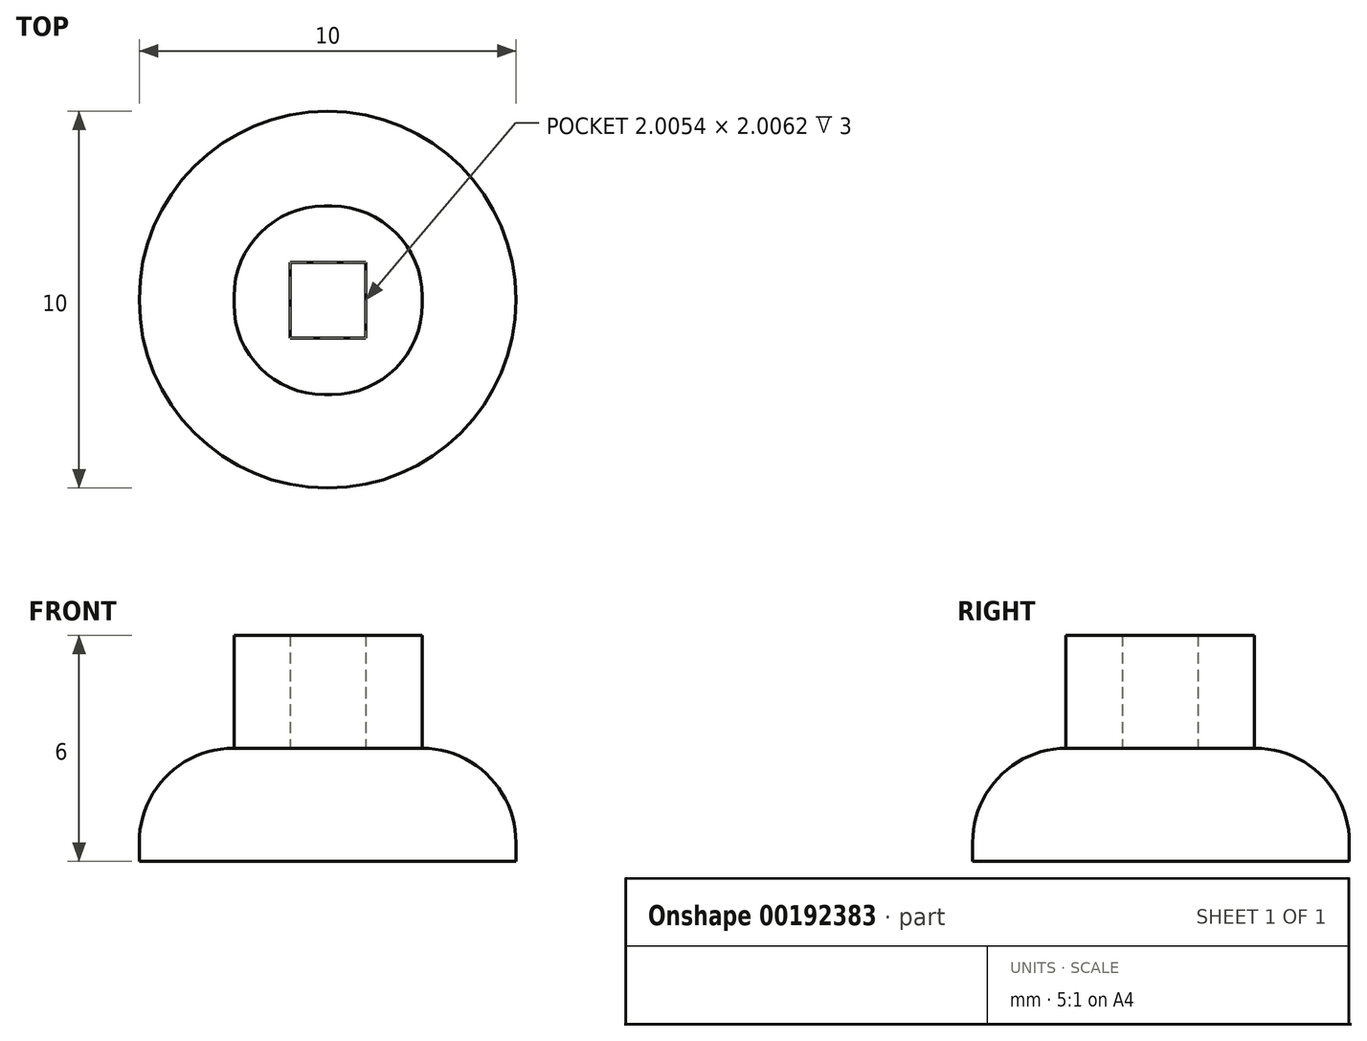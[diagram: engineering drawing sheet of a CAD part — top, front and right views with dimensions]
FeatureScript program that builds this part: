
annotation { "Feature Type Name" : "Feature", "Feature Type Description" : "" }
export const myFeature = defineFeature(function(context is Context, id is Id, definition is map)
    precondition{}
    {
        {
            var Q0;
            Q0=qCreatedBy(makeId("Top.planeOp"),FACE);
            var sketch = newSketch(context, id + "F0", { "sketchPlane" : qUnion([Q0])});
            skLineSegment(sketch, "E0.bottom", {"start": v(2.5, -2.5) * mm, "end": v(-2.5, -2.5) * mm});
            skLineSegment(sketch, "E0.top", {"start": v(2.5, 2.5) * mm, "end": v(-2.5, 2.5) * mm});
            skLineSegment(sketch, "E0.left", {"start": v(2.5, -2.5) * mm, "end": v(2.5, 2.5) * mm});
            skLineSegment(sketch, "E0.right", {"start": v(-2.5, -2.5) * mm, "end": v(-2.5, 2.5) * mm});
            skPoint(sketch, "E0.middle", {"position": v(0, 0) * mm});
            skLineSegment(sketch, "E1.bottom", {"start": v(1, -1) * mm, "end": v(-1, -1) * mm});
            skLineSegment(sketch, "E1.top", {"start": v(1, 1) * mm, "end": v(-1, 1) * mm});
            skLineSegment(sketch, "E1.left", {"start": v(1, -1) * mm, "end": v(1, 1) * mm});
            skLineSegment(sketch, "E1.right", {"start": v(-1, -1) * mm, "end": v(-1, 1) * mm});
            skCircle(sketch, "E2", {"center": v(-0.01, 0.02) * mm, "radius": 5 * mm});
            skSolve(sketch);
        }
        {
            var Q0;
            Q0=makeQuery(id+"F0.imprint","IMPRINT",FACE,{"disambiguationData":[TD([[makeQuery(id+"F0.imprint","IMPRINT",EDGE,{"derivedFrom":sQuery(id+"F0.wireOp",EDGE,"E0.bottom")}),1.0]])]});
            var Q1;
            Q1=makeQuery(id+"F0.imprint","IMPRINT",FACE,{"disambiguationData":[TD([[makeQuery(id+"F0.imprint","IMPRINT",EDGE,{"derivedFrom":sQuery(id+"F0.wireOp",EDGE,"E1.bottom")}),-1.0]])]});
            var Q2;
            Q2=makeQuery(id+"F0.imprint","IMPRINT",FACE,{"disambiguationData":[TD([[makeQuery(id+"F0.imprint","IMPRINT",EDGE,{"derivedFrom":sQuery(id+"F0.wireOp",EDGE,"E0.bottom")}),-1.0]])]});
            extrude(context, id + "F1", {"entities" : qUnion([Q0, Q1, Q2]), "depth" : 3 * mm});
        }
        {
            var Q0;
            Q0=makeQuery(id+"F1.opExtrude","CAP_FACE",FACE,{"disambiguationData":[OSD([sQuery(id+"F0.wireOp",EDGE,"E2")])],"isStart":false});
            var sketch = newSketch(context, id + "F2", { "sketchPlane" : qUnion([Q0])});
            skLineSegment(sketch, "E3.bottom", {"start": v(2.5, -2.5) * mm, "end": v(-2.5, -2.5) * mm});
            skLineSegment(sketch, "E3.top", {"start": v(2.5, 2.5) * mm, "end": v(-2.5, 2.5) * mm});
            skLineSegment(sketch, "E3.left", {"start": v(2.5, -2.5) * mm, "end": v(2.5, 2.5) * mm});
            skLineSegment(sketch, "E3.right", {"start": v(-2.5, -2.5) * mm, "end": v(-2.5, 2.5) * mm});
            skPoint(sketch, "E3.middle", {"position": v(0, 0) * mm});
            skLineSegment(sketch, "E4.bottom", {"start": v(1, -1) * mm, "end": v(-1, -1) * mm});
            skLineSegment(sketch, "E4.top", {"start": v(1, 1) * mm, "end": v(-1, 1) * mm});
            skLineSegment(sketch, "E4.left", {"start": v(1, -1) * mm, "end": v(1, 1) * mm});
            skLineSegment(sketch, "E4.right", {"start": v(-1, -1) * mm, "end": v(-1, 1) * mm});
            skSolve(sketch);
        }
        {
            var Q0;
            Q0=makeQuery(id+"F2.imprint","IMPRINT",FACE,{"disambiguationData":[TD([[makeQuery(id+"F2.imprint","IMPRINT",EDGE,{"derivedFrom":sQuery(id+"F2.wireOp",EDGE,"E3.bottom")}),-1.0]])]});
            extrude(context, id + "F3", {"entities" : qUnion([Q0]), "operationType" : NewBodyOperationType.ADD, "depth" : 3 * mm});
        }
        {
            var Q0;
            Q0=makeQuery(id+"F1.opExtrude","CAP_EDGE",EDGE,{"disambiguationData":[OSD([sQuery(id+"F0.wireOp",EDGE,"E2")])],"isStart":false});
            fillet(context, id + "F4", {"entities" : qUnion([Q0]), "radius" : 2.5 * mm, "tangentPropagation" : true, "allowEdgeOverflow" : false});
        }
        {
            var Q0;
            Q0=makeQuery(id+"F3.opExtrude","SWEPT_EDGE",EDGE,{"disambiguationData":[OSD([sQuery(id+"F2.wireOp",EDGE,"E3.top"),sQuery(id+"F2.wireOp",EDGE,"E3.right")])]});
            var Q1;
            Q1=makeQuery(id+"F3.opExtrude","SWEPT_EDGE",EDGE,{"disambiguationData":[OSD([sQuery(id+"F2.wireOp",EDGE,"E3.bottom"),sQuery(id+"F2.wireOp",EDGE,"E3.right")])]});
            var Q2;
            Q2=makeQuery(id+"F3.opExtrude","SWEPT_EDGE",EDGE,{"disambiguationData":[OSD([sQuery(id+"F2.wireOp",EDGE,"E3.bottom"),sQuery(id+"F2.wireOp",EDGE,"E3.left")])]});
            var Q3;
            Q3=makeQuery(id+"F3.opExtrude","SWEPT_EDGE",EDGE,{"disambiguationData":[OSD([sQuery(id+"F2.wireOp",EDGE,"E3.top"),sQuery(id+"F2.wireOp",EDGE,"E3.left")])]});
            fillet(context, id + "F5", {"entities" : qUnion([Q0, Q1, Q2, Q3]), "radius" : 2.4 * mm, "tangentPropagation" : true, "allowEdgeOverflow" : false});
        }
    });
